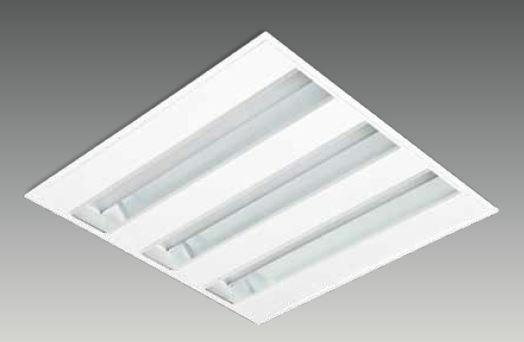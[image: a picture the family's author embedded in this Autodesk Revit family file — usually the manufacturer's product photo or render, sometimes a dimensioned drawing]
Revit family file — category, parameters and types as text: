
# Revit family: G 6060 OMA
name_source: partatom
category: Lighting Fixtures
revit_build: Autodesk Revit 2017 (Build: 20160225_1515(x64)
units: mm (PartAtom-declared; Revit-internal decimal feet)

## family parameters
Always vertical = Yes
Cut with Voids When Loaded = No
Host = Ceiling
Light Source = Yes
OmniClass Number = 23.80.70.11
OmniClass Title = Luminaries for Internal Lighting
Part Type = Normal
Room Calculation Point = No
Round Connector Dimension = Use Diameter
Shared = No

## types (4) — shared parameters
Color Filter = 16777215
Dimming Lamp Color Temperature Shift = <None>
Emit Shape Visible in Rendering = Yes
Emit from Rectangle Length = 570 mm  [stored 1.87008 ft]
Emit from Rectangle Width = 570 mm  [stored 1.87008 ft]
Light Source Symbol Size = 610 mm
Manufacturer = ARLIGHT
Type Image = G 6060 OMA.JPG

## per-type parameters (varying)
| type | Wattage Comments |
| GOMA.6060.42.30 | 42 |
| GOMA.6060.42.40 | 42 |
| GOMA.6060.37.30 | 37 |
| GOMA.6060.37.40 | 37 |

note: [stored X ft] marks values corroborated as IEEE doubles in the binary element streams (Revit-internal decimal feet)

## geometry (parser evidence)
native form markers: Sweep x2
no freeform markers — native parametric forms only
